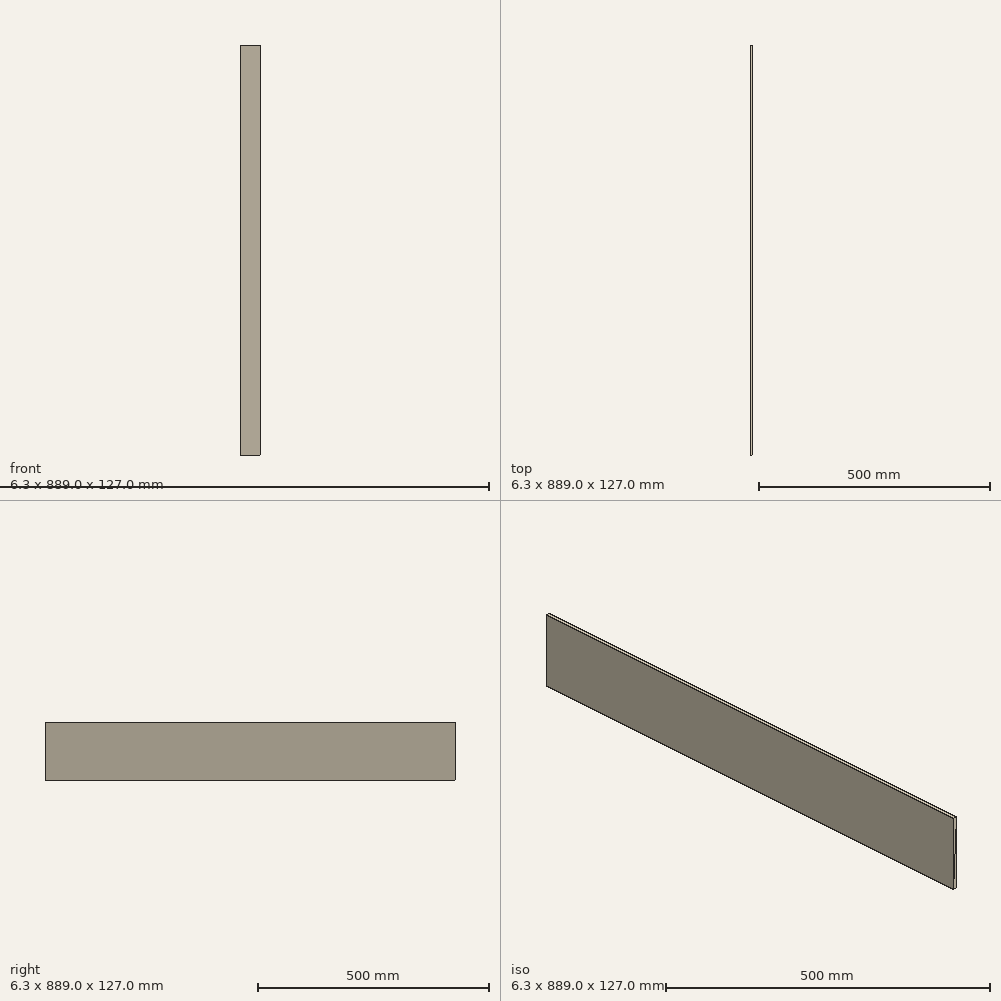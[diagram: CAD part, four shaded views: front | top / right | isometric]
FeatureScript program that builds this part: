
annotation { "Feature Type Name" : "Feature", "Feature Type Description" : "" }
export const myFeature = defineFeature(function(context is Context, id is Id, definition is map)
    precondition{}
    {
        {
            var Q0;
            Q0=qCreatedBy(makeId("Right.planeOp"),FACE);
            var sketch = newSketch(context, id + "F0", { "sketchPlane" : qUnion([Q0])});
            skLineSegment(sketch, "E0.bottom", {"start": v(444.5, 63.5) * mm, "end": v(-444.5, 63.5) * mm});
            skLineSegment(sketch, "E0.top", {"start": v(444.5, -63.5) * mm, "end": v(-444.5, -63.5) * mm});
            skLineSegment(sketch, "E0.left", {"start": v(444.5, 63.5) * mm, "end": v(444.5, -63.5) * mm});
            skLineSegment(sketch, "E0.right", {"start": v(-444.5, 63.5) * mm, "end": v(-444.5, -63.5) * mm});
            skPoint(sketch, "E0.middle", {"position": v(0, 0) * mm});
            skPoint(sketch, "E1.snap10", {"position": v(-444.5, 0) * mm});
            skPoint(sketch, "E1.1.internal.orphan", {"position": v(-593.32, 0) * mm});
            skPoint(sketch, "E2.MirrorCS.end.orphan", {"position": v(444.5, 63.5) * mm});
            skPoint(sketch, "E2.MirrorCS.start.orphan", {"position": v(444.5, -63.5) * mm});
            skPoint(sketch, "E3.start.orphan", {"position": v(444.5, 0) * mm});
            skSolve(sketch);
        }
        {
            var Q0;
            Q0 = qSketchRegion(id + "F0", true);
            extrude(context, id + "F1", {"entities" : qUnion([Q0]), "depth" : 6.35 * mm, "offsetDistance" : 25.4 * mm});
        }
        {
            var Q0;
            {var subQ0=sQuery(id+"F0.wireOp",EDGE,"E0.top");Q0=makeQuery(id+"F0.imprint","IMPRINT",FACE,{"disambiguationData":[TD([[makeQuery(id+"F0.imprint","IMPRINT",EDGE,{"derivedFrom":subQ0}),-1.0]])]});}
            extrude(context, id + "F2", {"entities" : qUnion([Q0]), "depth" : 6.35 * mm, "offsetDistance" : 25.4 * mm});
        }
    });
